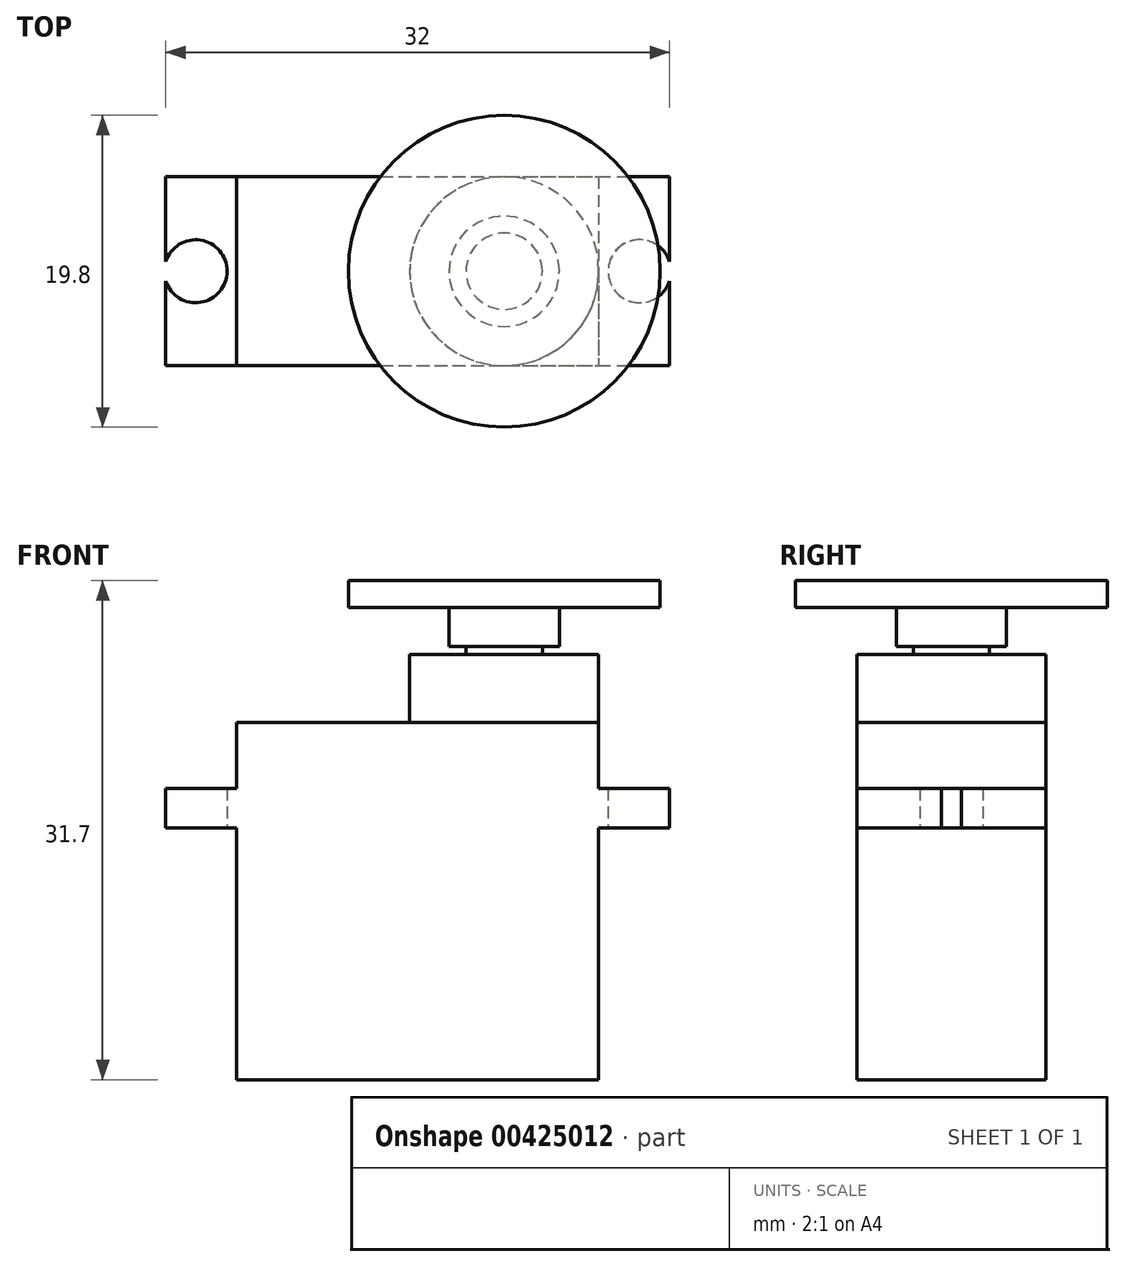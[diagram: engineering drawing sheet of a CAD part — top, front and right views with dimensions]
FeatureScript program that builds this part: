
annotation { "Feature Type Name" : "Feature", "Feature Type Description" : "" }
export const myFeature = defineFeature(function(context is Context, id is Id, definition is map)
    precondition{}
    {
        {
            var Q0;
            Q0=qCreatedBy(makeId("Top.planeOp"),FACE);
            var sketch = newSketch(context, id + "F0", { "sketchPlane" : qUnion([Q0])});
            skLineSegment(sketch, "E0.bottom", {"start": v(-17, 6) * mm, "end": v(6, 6) * mm});
            skLineSegment(sketch, "E0.top", {"start": v(-17, -6) * mm, "end": v(6, -6) * mm});
            skLineSegment(sketch, "E0.left", {"start": v(-17, 6) * mm, "end": v(-17, -6) * mm});
            skLineSegment(sketch, "E0.right", {"start": v(6, 6) * mm, "end": v(6, -6) * mm});
            skCircle(sketch, "E1", {"center": v(0, 0) * mm, "radius": 6 * mm});
            skCircle(sketch, "E2", {"center": v(0, 0) * mm, "radius": 2.43 * mm});
            skLineSegment(sketch, "E3.bottom", {"start": v(6, 6) * mm, "end": v(10.5, 6) * mm});
            skLineSegment(sketch, "E3.top", {"start": v(6, -6) * mm, "end": v(10.5, -6) * mm});
            skLineSegment(sketch, "E3.right", {"start": v(10.5, 6) * mm, "end": v(10.5, 0.62) * mm});
            skLineSegment(sketch, "E4.bottom", {"start": v(-17, 6) * mm, "end": v(-21.5, 6) * mm});
            skLineSegment(sketch, "E4.top", {"start": v(-17, -6) * mm, "end": v(-21.5, -6) * mm});
            skLineSegment(sketch, "E4.right", {"start": v(-21.5, 6) * mm, "end": v(-21.5, 0.62) * mm});
            skArc(sketch, "E5", {"start": v(-21.5, -0.62) * mm, "mid": v(-17.6, 0) * mm, "end": v(-21.5, 0.62) * mm});
            skLineSegment(sketch, "E6", {"start": v(-5.5, 11.77) * mm, "end": v(-5.5, -13.9) * mm, "construction": true});
            skPoint(sketch, "E6.startSnap0", {"position": v(-5.5, 6) * mm});
            skArc(sketch, "E7.MirrorC", {"start": v(10.5, -0.62) * mm, "mid": v(6.6, 0) * mm, "end": v(10.5, 0.62) * mm});
            skLineSegment(sketch, "E8.trimOffspring", {"start": v(-21.5, -0.62) * mm, "end": v(-21.5, -6) * mm});
            skLineSegment(sketch, "E9.trimOffspring", {"start": v(10.5, -0.62) * mm, "end": v(10.5, -6) * mm});
            skSolve(sketch);
        }
        {
            var Q0;
            {var subQ0=sQuery(id+"F0.wireOp",EDGE,"E0.left");Q0=makeQuery(id+"F0.imprint","IMPRINT",FACE,{"disambiguationData":[TD([[makeQuery(id+"F0.imprint","IMPRINT",EDGE,{"derivedFrom":subQ0}),1.0]])]});}
            var Q1;
            Q1=makeQuery(id+"F0.imprint","IMPRINT",FACE,{"disambiguationData":[TD([[makeQuery(id+"F0.imprint","IMPRINT",EDGE,{"derivedFrom":sQuery(id+"F0.wireOp",EDGE,"E2")}),-1.0]])]});
            var Q2;
            Q2=makeQuery(id+"F0.imprint","IMPRINT",FACE,{"disambiguationData":[TD([[makeQuery(id+"F0.imprint","IMPRINT",EDGE,{"derivedFrom":sQuery(id+"F0.wireOp",EDGE,"E2")}),1.0]])]});
            var Q3;
            {var subQ1=sQuery(id+"F0.wireOp",EDGE,"E0.bottom");var subQ3=sQuery(id+"F0.wireOp",EDGE,"E1");var subQ4=makeQuery(id+"F0.imprint","INTERSECT",VERTEX,{"derivedFrom":[subQ1,subQ3]});Q3=makeQuery(id+"F0.imprint","IMPRINT",FACE,{"disambiguationData":[TD([[makeQuery(id+"F0.imprint","IMPRINT",EDGE,{"disambiguationData":[TD([[subQ4,1.0]])],"derivedFrom":subQ3}),-1.0]])]});}
            var Q4;
            {var subQ1=sQuery(id+"F0.wireOp",EDGE,"E0.top");var subQ3=sQuery(id+"F0.wireOp",EDGE,"E1");var subQ4=makeQuery(id+"F0.imprint","INTERSECT",VERTEX,{"derivedFrom":[subQ1,subQ3]});Q4=makeQuery(id+"F0.imprint","IMPRINT",FACE,{"disambiguationData":[TD([[makeQuery(id+"F0.imprint","IMPRINT",EDGE,{"disambiguationData":[TD([[subQ4,-1.0]])],"derivedFrom":subQ3}),-1.0]])]});}
            extrude(context, id + "F1", {"entities" : qUnion([Q0, Q1, Q2, Q3, Q4]), "oppositeDirection" : true, "depth" : 16 * mm, "hasSecondDirection" : true, "secondDirectionOppositeDirection" : false, "secondDirectionDepth" : (22.7 - 16) * mm});
        }
        {
            var Q0;
            Q0=makeQuery(id+"F0.imprint","IMPRINT",FACE,{"disambiguationData":[TD([[makeQuery(id+"F0.imprint","IMPRINT",EDGE,{"derivedFrom":sQuery(id+"F0.wireOp",EDGE,"E4.bottom")}),1.0]])]});
            var Q1;
            {var subQ3=sQuery(id+"F0.wireOp",EDGE,"E3.bottom");Q1=makeQuery(id+"F0.imprint","IMPRINT",FACE,{"disambiguationData":[TD([[makeQuery(id+"F0.imprint","IMPRINT",EDGE,{"derivedFrom":subQ3}),-1.0]])]});}
            extrude(context, id + "F2", {"entities" : qUnion([Q0, Q1]), "operationType" : NewBodyOperationType.ADD, "depth" : 2.5 * mm});
        }
        {
            var Q0;
            Q0=makeQuery(id+"F0.imprint","IMPRINT",FACE,{"disambiguationData":[TD([[makeQuery(id+"F0.imprint","IMPRINT",EDGE,{"derivedFrom":sQuery(id+"F0.wireOp",EDGE,"E2")}),-1.0]])]});
            var Q1;
            Q1=makeQuery(id+"F0.imprint","IMPRINT",FACE,{"disambiguationData":[TD([[makeQuery(id+"F0.imprint","IMPRINT",EDGE,{"derivedFrom":sQuery(id+"F0.wireOp",EDGE,"E2")}),1.0]])]});
            extrude(context, id + "F3", {"entities" : qUnion([Q0, Q1]), "operationType" : NewBodyOperationType.ADD, "depth" : 11 * mm});
        }
        {
            var Q0;
            Q0=makeQuery(id+"F0.imprint","IMPRINT",FACE,{"disambiguationData":[TD([[makeQuery(id+"F0.imprint","IMPRINT",EDGE,{"derivedFrom":sQuery(id+"F0.wireOp",EDGE,"E2")}),1.0]])]});
            extrude(context, id + "F4", {"entities" : qUnion([Q0]), "operationType" : NewBodyOperationType.ADD, "depth" : (11 + 3) * mm});
        }
        {
            var Q0;
            Q0=makeQuery(id+"F4.opExtrude","CAP_FACE",FACE,{"disambiguationData":[OSD([sQuery(id+"F0.wireOp",EDGE,"E2")])],"isStart":false});
            var sketch = newSketch(context, id + "F5", { "sketchPlane" : qUnion([Q0])});
            skCircle(sketch, "E10.0", {"center": v(0, 0) * mm, "radius": 2.43 * mm});
            skCircle(sketch, "E11", {"center": v(0, 0) * mm, "radius": 3.5 * mm});
            skCircle(sketch, "E12", {"center": v(0, 0) * mm, "radius": 9.9 * mm});
            skSolve(sketch);
        }
        {
            var Q0;
            Q0=makeQuery(id+"F5.imprint","IMPRINT",FACE,{"disambiguationData":[TD([[makeQuery(id+"F5.imprint","IMPRINT",EDGE,{"derivedFrom":sQuery(id+"F5.wireOp",EDGE,"E10.0")}),-1.0]])]});
            extrude(context, id + "F6", {"entities" : qUnion([Q0]), "oppositeDirection" : true, "depth" : 2.5 * mm});
        }
        {
            var Q0;
            Q0=makeQuery(id+"F5.imprint","IMPRINT",FACE,{"disambiguationData":[TD([[makeQuery(id+"F5.imprint","IMPRINT",EDGE,{"derivedFrom":sQuery(id+"F5.wireOp",EDGE,"E11")}),-1.0]])]});
            var Q1;
            Q1=makeQuery(id+"F5.imprint","IMPRINT",FACE,{"disambiguationData":[TD([[makeQuery(id+"F5.imprint","IMPRINT",EDGE,{"derivedFrom":sQuery(id+"F5.wireOp",EDGE,"E10.0")}),-1.0]])]});
            var Q2;
            Q2=makeQuery(id+"F5.imprint","IMPRINT",FACE,{"disambiguationData":[TD([[makeQuery(id+"F5.imprint","IMPRINT",EDGE,{"derivedFrom":sQuery(id+"F5.wireOp",EDGE,"E10.0")}),1.0]])]});
            extrude(context, id + "F7", {"entities" : qUnion([Q0, Q1, Q2]), "operationType" : NewBodyOperationType.ADD, "depth" : 1.7 * mm});
        }
    });
